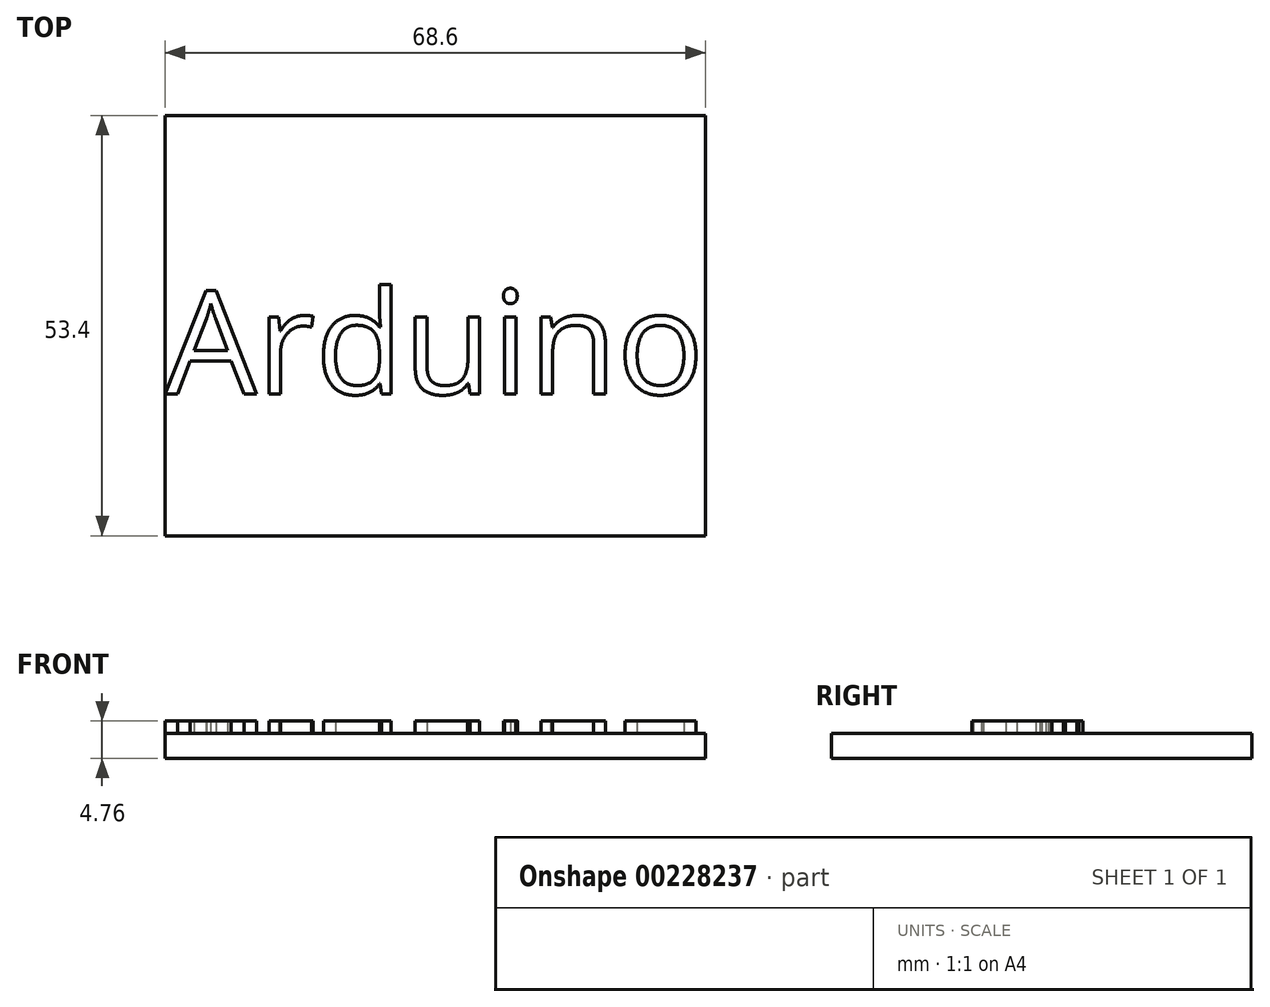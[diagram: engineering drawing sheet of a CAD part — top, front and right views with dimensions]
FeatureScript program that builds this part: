
annotation { "Feature Type Name" : "Feature", "Feature Type Description" : "" }
export const myFeature = defineFeature(function(context is Context, id is Id, definition is map)
    precondition{}
    {
        {
            var Q0;
            Q0=qCreatedBy(makeId("Top.planeOp"),FACE);
            var sketch = newSketch(context, id + "F0", { "sketchPlane" : qUnion([Q0])});
            skLineSegment(sketch, "E0.bottom", {"start": v(-34.3, 26.7) * mm, "end": v(34.3, 26.7) * mm});
            skLineSegment(sketch, "E0.top", {"start": v(-34.3, -26.7) * mm, "end": v(34.3, -26.7) * mm});
            skLineSegment(sketch, "E0.left", {"start": v(-34.3, 26.7) * mm, "end": v(-34.3, -26.7) * mm});
            skLineSegment(sketch, "E0.right", {"start": v(34.3, 26.7) * mm, "end": v(34.3, -26.7) * mm});
            skPoint(sketch, "E0.middle", {"position": v(0, 0) * mm});
            skSolve(sketch);
        }
        {
            var Q0;
            Q0=makeQuery(id+"F0.imprint","IMPRINT",FACE,{"disambiguationData":[TD([[makeQuery(id+"F0.imprint","IMPRINT",EDGE,{"derivedFrom":sQuery(id+"F0.wireOp",EDGE,"E0.bottom")}),-1.0]])]});
            extrude(context, id + "F1", {"entities" : qUnion([Q0]), "depth" : 3.17 * mm});
        }
        {
            var Q0;
            Q0=makeQuery(id+"F1.opExtrude","CAP_FACE",FACE,{"disambiguationData":[OSD([sQuery(id+"F0.wireOp",EDGE,"E0.bottom"),sQuery(id+"F0.wireOp",EDGE,"E0.top"),sQuery(id+"F0.wireOp",EDGE,"E0.left"),sQuery(id+"F0.wireOp",EDGE,"E0.right")])],"isStart":false});
            var sketch = newSketch(context, id + "F2", { "sketchPlane" : qUnion([Q0])});
            skText(sketch, "E1", { "text": "Arduino \n", "fontName": "OpenSans-Regular.ttf"});
            const initialGuessF2  = {"E1": [-0.0343, -0.00867, 1, 0, 0.01318]};
            skSetInitialGuess(sketch, initialGuessF2);
            skSolve(sketch);
        }
        {
            var Q0;
            Q0 = qSketchRegion(id + "F2", true);
            extrude(context, id + "F3", {"entities" : qUnion([Q0]), "operationType" : NewBodyOperationType.ADD, "depth" : 1.59 * mm});
        }
    });
